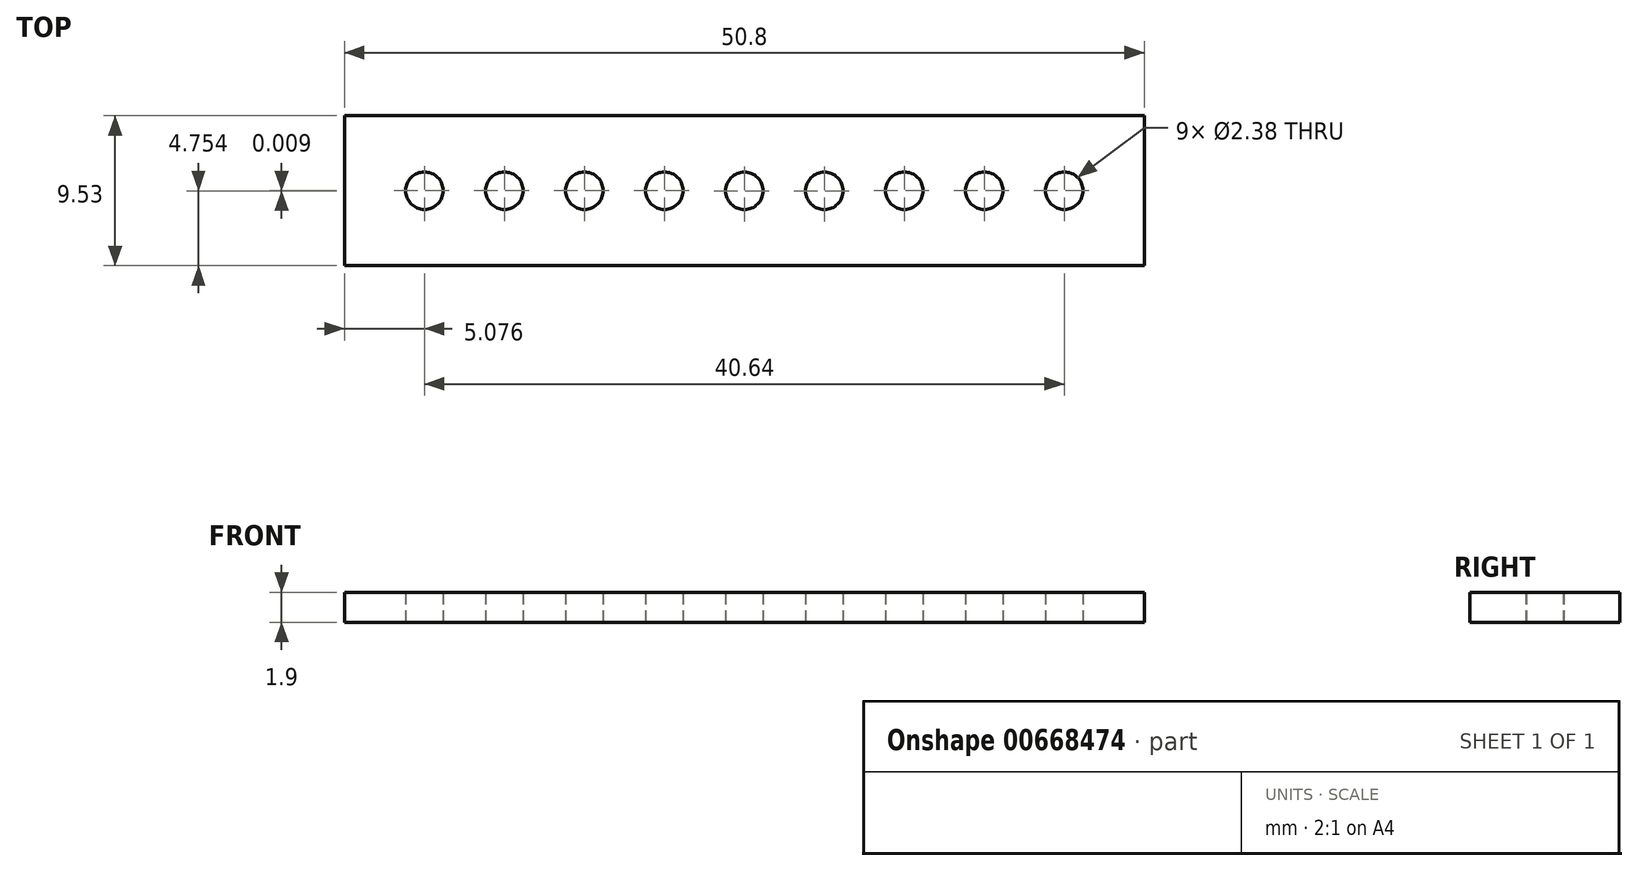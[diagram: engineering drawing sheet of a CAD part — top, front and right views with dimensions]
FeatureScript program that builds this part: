
annotation { "Feature Type Name" : "Feature", "Feature Type Description" : "" }
export const myFeature = defineFeature(function(context is Context, id is Id, definition is map)
    precondition{}
    {
        {
            var Q0;
            Q0=qCreatedBy(makeId("Top.planeOp"),FACE);
            var sketch = newSketch(context, id + "F0", { "sketchPlane" : qUnion([Q0])});
            skLineSegment(sketch, "E0.bottom", {"start": v(-39.65, 17.64) * mm, "end": v(11.15, 17.64) * mm});
            skLineSegment(sketch, "E0.top", {"start": v(-39.65, 8.11) * mm, "end": v(11.15, 8.11) * mm});
            skLineSegment(sketch, "E0.left", {"start": v(-39.65, 17.64) * mm, "end": v(-39.65, 8.11) * mm});
            skLineSegment(sketch, "E0.right", {"start": v(11.15, 17.64) * mm, "end": v(11.15, 8.11) * mm});
            skCircle(sketch, "E1", {"center": v(-34.57, 12.87) * mm, "radius": 1.19 * mm});
            skCircle(sketch, "E2", {"center": v(-29.5, 12.87) * mm, "radius": 1.19 * mm});
            skCircle(sketch, "E3", {"center": v(-24.41, 12.87) * mm, "radius": 1.19 * mm});
            skCircle(sketch, "E4", {"center": v(-19.33, 12.87) * mm, "radius": 1.19 * mm});
            skCircle(sketch, "E5", {"center": v(-14.25, 12.86) * mm, "radius": 1.19 * mm});
            skCircle(sketch, "E6", {"center": v(-9.17, 12.86) * mm, "radius": 1.19 * mm});
            skCircle(sketch, "E7", {"center": v(-4.1, 12.87) * mm, "radius": 1.19 * mm});
            skCircle(sketch, "E8", {"center": v(0.99, 12.87) * mm, "radius": 1.19 * mm});
            skCircle(sketch, "E9", {"center": v(6.07, 12.87) * mm, "radius": 1.19 * mm});
            skPoint(sketch, "E10.orphan", {"position": v(11.15, 12.87) * mm});
            skPoint(sketch, "E11.start.orphan", {"position": v(-39.65, 12.87) * mm});
            skSolve(sketch);
        }
        {
            var Q0;
            Q0=makeQuery(id+"F0.imprint","IMPRINT",FACE,{"disambiguationData":[TD([[makeQuery(id+"F0.imprint","IMPRINT",EDGE,{"derivedFrom":sQuery(id+"F0.wireOp",EDGE,"E0.bottom")}),-1.0]])]});
            extrude(context, id + "F1", {"entities" : qUnion([Q0]), "depth" : 1.9 * mm});
        }
    });
